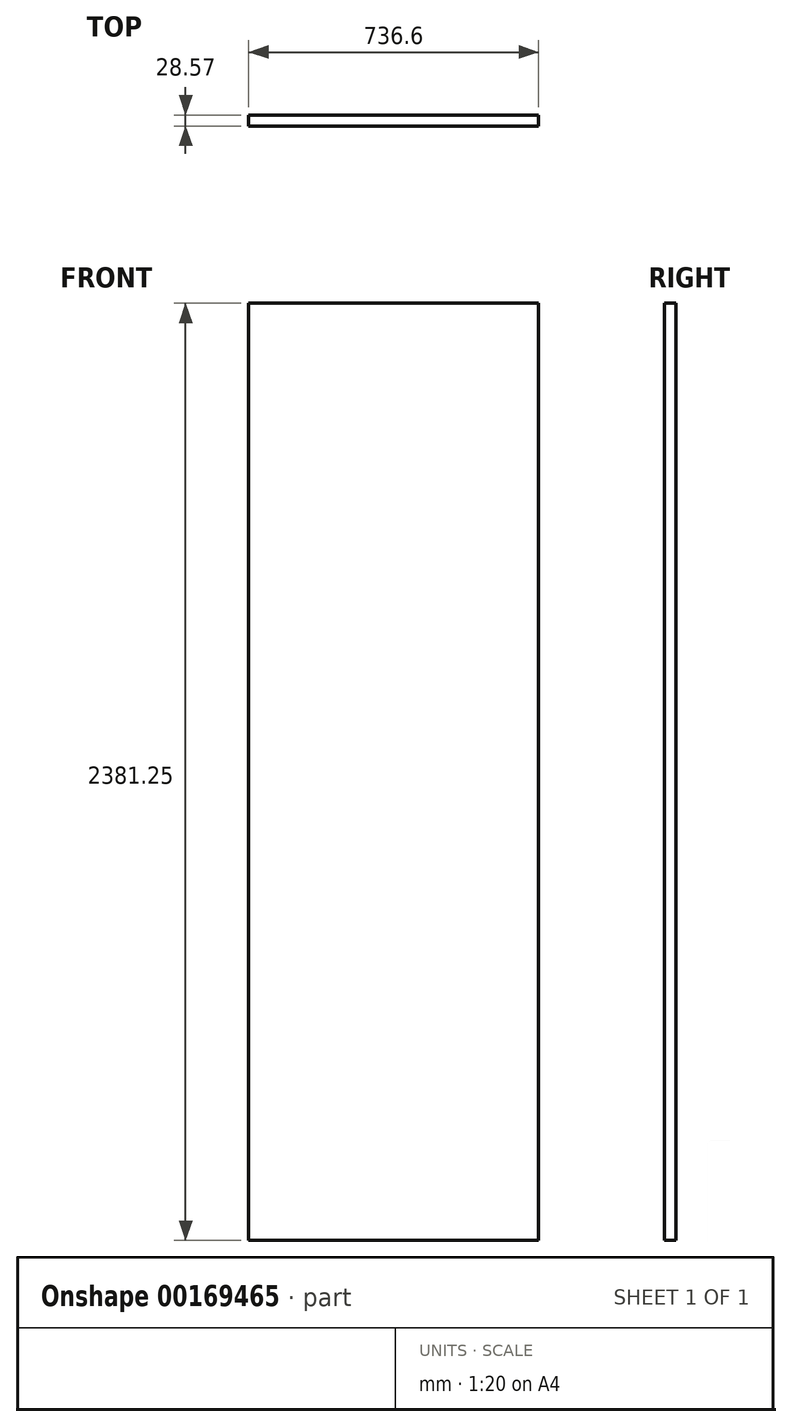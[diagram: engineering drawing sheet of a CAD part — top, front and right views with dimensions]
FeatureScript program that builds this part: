
annotation { "Feature Type Name" : "Feature", "Feature Type Description" : "" }
export const myFeature = defineFeature(function(context is Context, id is Id, definition is map)
    precondition{}
    {
        {
            var Q0;
            Q0=qCreatedBy(makeId("Front.planeOp"),FACE);
            var sketch = newSketch(context, id + "F0", { "sketchPlane" : qUnion([Q0])});
            skLineSegment(sketch, "E0.bottom", {"start": v(-323.17, 1747.43) * mm, "end": v(413.43, 1747.43) * mm});
            skLineSegment(sketch, "E0.top", {"start": v(-323.17, -633.82) * mm, "end": v(413.43, -633.82) * mm});
            skLineSegment(sketch, "E0.left", {"start": v(-323.17, 1747.43) * mm, "end": v(-323.17, -633.82) * mm});
            skLineSegment(sketch, "E0.right", {"start": v(413.43, 1747.43) * mm, "end": v(413.43, -633.82) * mm});
            skSolve(sketch);
        }
        {
            var Q0;
            Q0 = qSketchRegion(id + "F0", true);
            extrude(context, id + "F1", {"entities" : qUnion([Q0]), "depth" : 28.57 * mm});
        }
    });
